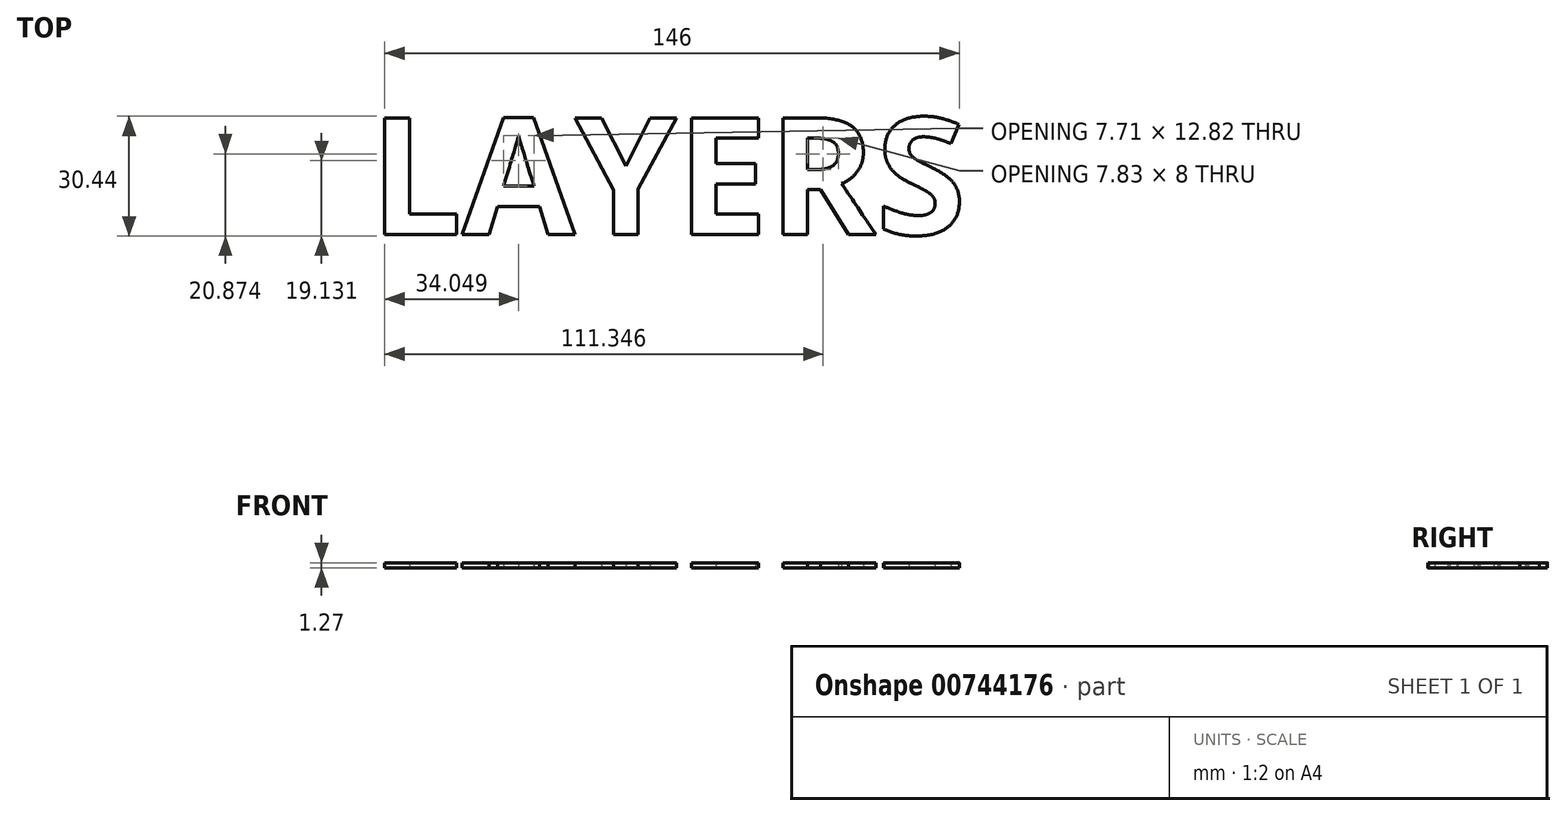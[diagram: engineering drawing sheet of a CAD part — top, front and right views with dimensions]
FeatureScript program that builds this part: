
annotation { "Feature Type Name" : "Feature", "Feature Type Description" : "" }
export const myFeature = defineFeature(function(context is Context, id is Id, definition is map)
    precondition{}
    {
        {
            var Q0;
            Q0=qCreatedBy(makeId("Top.planeOp"),FACE);
            var sketch = newSketch(context, id + "F0", { "sketchPlane" : qUnion([Q0])});
            skText(sketch, "E0", { "text": "LAYERS", "fontName": "OpenSans-Bold.ttf"});
            const initialGuessF0  = {"E0": [-0.04567, -0.01139, 1, 0, 0.02986]};
            skSetInitialGuess(sketch, initialGuessF0);
            skSolve(sketch);
        }
        {
            var Q0;
            Q0 = qSketchRegion(id + "F0", true);
            extrude(context, id + "F1", {"entities" : qUnion([Q0]), "depth" : 1.27 * mm, "offsetDistance" : 25.4 * mm});
        }
    });
